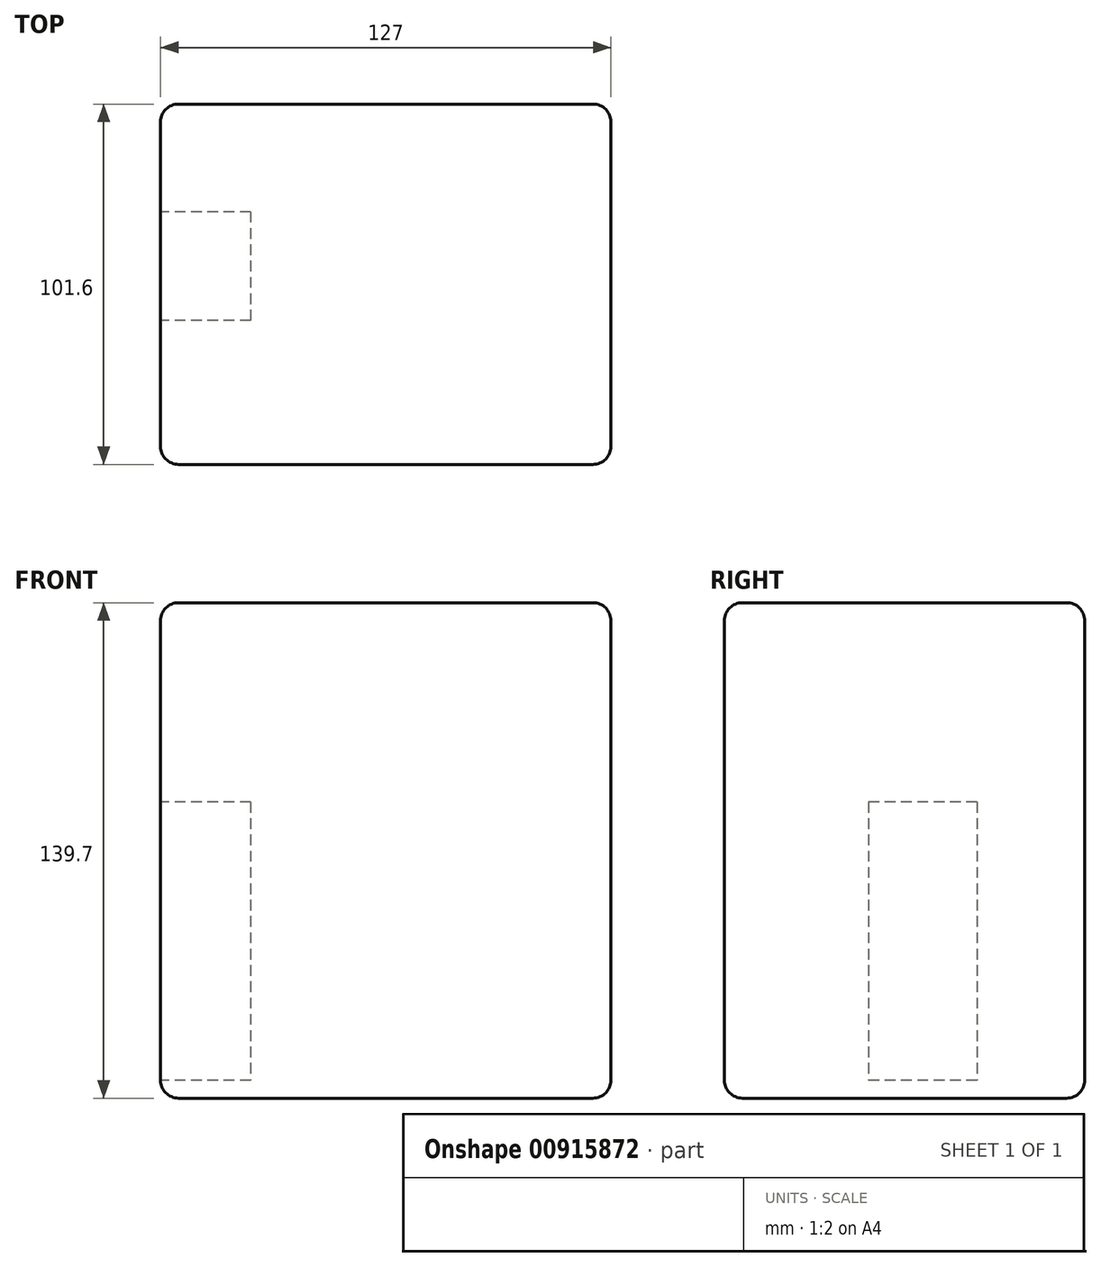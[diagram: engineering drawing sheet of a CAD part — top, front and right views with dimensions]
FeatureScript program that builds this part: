
annotation { "Feature Type Name" : "Feature", "Feature Type Description" : "" }
export const myFeature = defineFeature(function(context is Context, id is Id, definition is map)
    precondition{}
    {
        {
            var Q0;
            Q0=qCreatedBy(makeId("Top.planeOp"),FACE);
            var sketch = newSketch(context, id + "F0", { "sketchPlane" : qUnion([Q0])});
            skLineSegment(sketch, "E0.bottom", {"start": v(0, 0) * mm, "end": v(127, 0) * mm});
            skLineSegment(sketch, "E0.top", {"start": v(0, -101.6) * mm, "end": v(127, -101.6) * mm});
            skLineSegment(sketch, "E0.left", {"start": v(0, 0) * mm, "end": v(0, -101.6) * mm});
            skLineSegment(sketch, "E0.right", {"start": v(127, 0) * mm, "end": v(127, -101.6) * mm});
            skSolve(sketch);
        }
        {
            var Q0;
            Q0 = qSketchRegion(id + "F0", true);
            extrude(context, id + "F1", {"entities" : qUnion([Q0]), "depth" : 139.7 * mm, "offsetDistance" : 25.4 * mm});
        }
        {
            var Q0;
            Q0=makeQuery(id+"F1.opExtrude","CAP_EDGE",EDGE,{"disambiguationData":[OSD([sQuery(id+"F0.wireOp",EDGE,"E0.top")])],"isStart":false});
            var Q1;
            Q1=makeQuery(id+"F1.opExtrude","CAP_EDGE",EDGE,{"disambiguationData":[OSD([sQuery(id+"F0.wireOp",EDGE,"E0.right")])],"isStart":false});
            var Q2;
            Q2=makeQuery(id+"F1.opExtrude","SWEPT_EDGE",EDGE,{"disambiguationData":[OSD([sQuery(id+"F0.wireOp",EDGE,"E0.top"),sQuery(id+"F0.wireOp",EDGE,"E0.right")])]});
            var Q3;
            Q3=makeQuery(id+"F1.opExtrude","CAP_EDGE",EDGE,{"disambiguationData":[OSD([sQuery(id+"F0.wireOp",EDGE,"E0.left")])],"isStart":false});
            var Q4;
            Q4=makeQuery(id+"F1.opExtrude","SWEPT_EDGE",EDGE,{"disambiguationData":[OSD([sQuery(id+"F0.wireOp",EDGE,"E0.top"),sQuery(id+"F0.wireOp",EDGE,"E0.left")])]});
            var Q5;
            Q5=makeQuery(id+"F1.opExtrude","SWEPT_FACE",FACE,{"disambiguationData":[OSD([sQuery(id+"F0.wireOp",EDGE,"E0.bottom")])]});
            var Q6;
            Q6=makeQuery(id+"F1.opExtrude","SWEPT_FACE",FACE,{"disambiguationData":[OSD([sQuery(id+"F0.wireOp",EDGE,"E0.right")])]});
            var Q7;
            Q7=makeQuery(id+"F1.opExtrude","CAP_FACE",FACE,{"disambiguationData":[OSD([sQuery(id+"F0.wireOp",EDGE,"E0.bottom"),sQuery(id+"F0.wireOp",EDGE,"E0.top"),sQuery(id+"F0.wireOp",EDGE,"E0.left"),sQuery(id+"F0.wireOp",EDGE,"E0.right")])],"isStart":true});
            fillet(context, id + "F2", {"entities" : qUnion([Q0, Q1, Q2, Q3, Q4, Q5, Q6, Q7]), "radius" : 5.08 * mm, "tangentPropagation" : true, "allowEdgeOverflow" : false});
        }
        {
            var Q0;
            Q0=makeQuery(id+"F1.opExtrude","SWEPT_FACE",FACE,{"disambiguationData":[OSD([sQuery(id+"F0.wireOp",EDGE,"E0.left")])]});
            var sketch = newSketch(context, id + "F3", { "sketchPlane" : qUnion([Q0])});
            skLineSegment(sketch, "E1.bottom", {"start": v(30.39, 83.53) * mm, "end": v(61.02, 83.53) * mm});
            skLineSegment(sketch, "E1.top", {"start": v(30.39, -35.1) * mm, "end": v(61.02, -35.1) * mm});
            skLineSegment(sketch, "E1.left", {"start": v(30.39, 83.53) * mm, "end": v(30.39, -35.1) * mm});
            skLineSegment(sketch, "E1.right", {"start": v(61.02, 83.53) * mm, "end": v(61.02, -35.1) * mm});
            skSolve(sketch);
        }
        {
            var Q0;
            {var subQ0=sQuery(id+"F3.wireOp",EDGE,"E1.bottom");Q0=makeQuery(id+"F3.imprint","IMPRINT",FACE,{"disambiguationData":[TD([[makeQuery(id+"F3.imprint","IMPRINT",EDGE,{"derivedFrom":subQ0}),-1.0]])]});}
            extrude(context, id + "F4", {"entities" : qUnion([Q0]), "operationType" : NewBodyOperationType.REMOVE, "oppositeDirection" : true, "depth" : 25.4 * mm, "offsetDistance" : 25.4 * mm});
        }
    });
